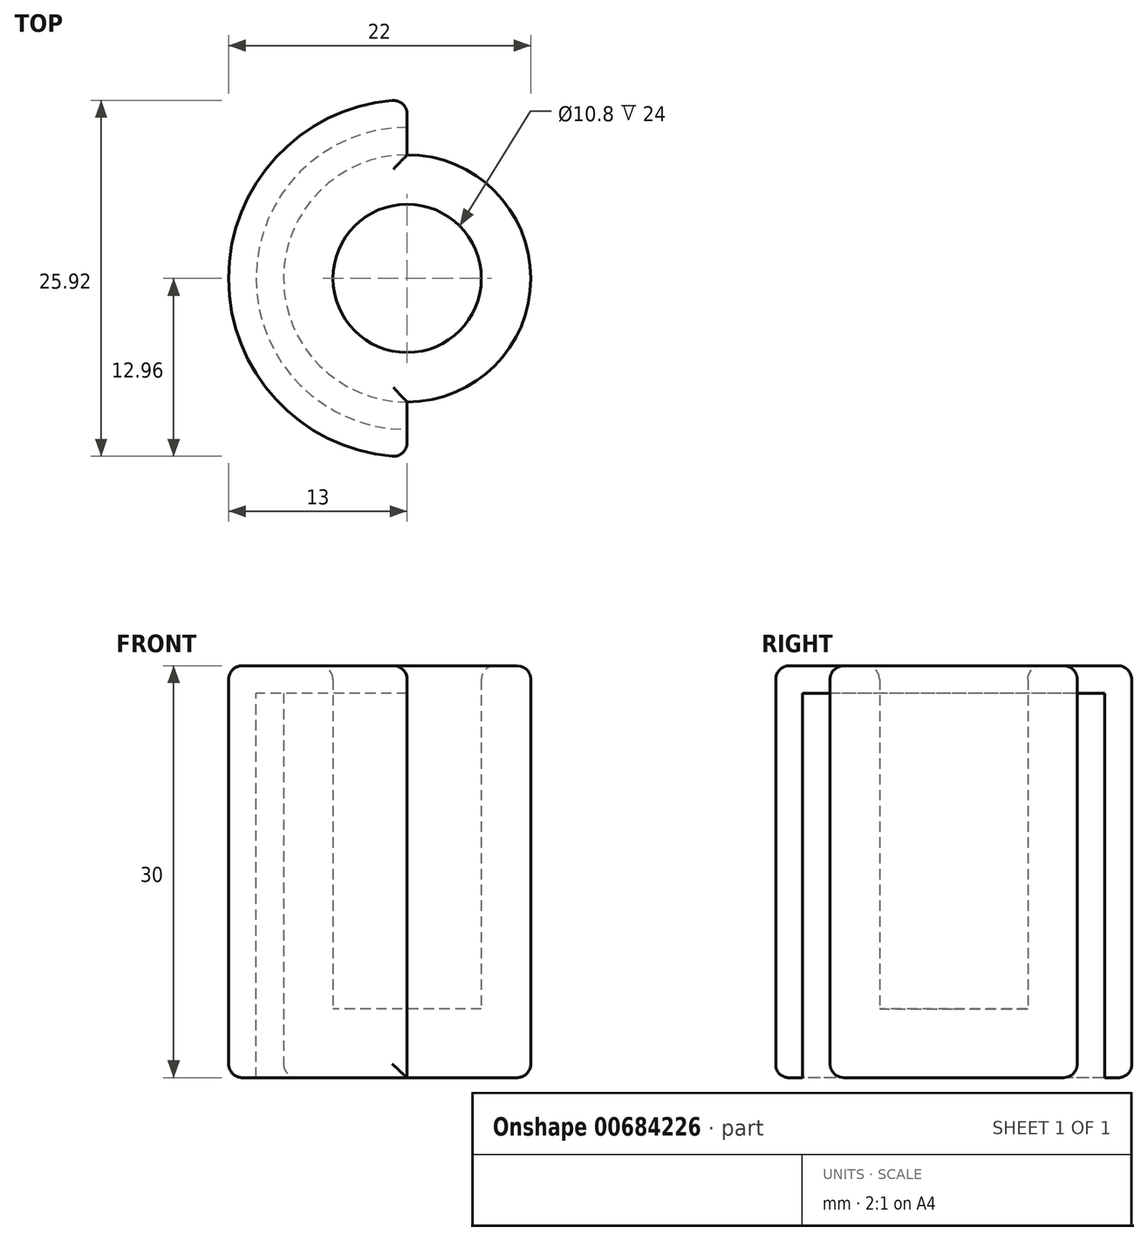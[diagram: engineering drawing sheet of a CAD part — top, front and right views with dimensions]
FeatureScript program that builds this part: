
annotation { "Feature Type Name" : "Feature", "Feature Type Description" : "" }
export const myFeature = defineFeature(function(context is Context, id is Id, definition is map)
    precondition{}
    {
        {
            var Q0;
            Q0=qCreatedBy(makeId("Top.planeOp"),FACE);
            var sketch = newSketch(context, id + "F0", { "sketchPlane" : qUnion([Q0])});
            skCircle(sketch, "E0", {"center": v(0, 0) * mm, "radius": 9 * mm});
            skCircle(sketch, "E1", {"center": v(0, 0) * mm, "radius": 5.4 * mm});
            skSolve(sketch);
        }
        {
            var Q0;
            Q0=makeQuery(id+"F0.imprint","IMPRINT",FACE,{"disambiguationData":[TD([[makeQuery(id+"F0.imprint","IMPRINT",EDGE,{"derivedFrom":sQuery(id+"F0.wireOp",EDGE,"E0")}),1.0]])]});
            extrude(context, id + "F1", {"entities" : qUnion([Q0]), "depth" : 30 * mm, "offsetDistance" : 25 * mm});
        }
        {
            var Q0;
            Q0=makeQuery(id+"F0.imprint","IMPRINT",FACE,{"disambiguationData":[TD([[makeQuery(id+"F0.imprint","IMPRINT",EDGE,{"derivedFrom":sQuery(id+"F0.wireOp",EDGE,"E1")}),1.0]])]});
            extrude(context, id + "F2", {"entities" : qUnion([Q0]), "operationType" : NewBodyOperationType.ADD, "depth" : 5 * mm, "offsetDistance" : 25 * mm});
        }
        {
            var Q0;
            Q0=makeQuery(id+"F1.opExtrude","CAP_FACE",FACE,{"disambiguationData":[OSD([sQuery(id+"F0.wireOp",EDGE,"E0"),sQuery(id+"F0.wireOp",EDGE,"E1")])],"isStart":false});
            var sketch = newSketch(context, id + "F3", { "sketchPlane" : qUnion([Q0])});
            skArc(sketch, "E2", {"start": v(0, 13) * mm, "mid": v(-13, 0) * mm, "end": v(0, -13) * mm});
            skArc(sketch, "E3", {"start": v(0, 11) * mm, "mid": v(-11, 0) * mm, "end": v(0, -11) * mm});
            skLineSegment(sketch, "E4", {"start": v(0, -13) * mm, "end": v(0, -9) * mm});
            skLineSegment(sketch, "E5", {"start": v(0, 13) * mm, "end": v(0, 9) * mm});
            skSolve(sketch);
        }
        {
            var Q0;
            Q0=makeQuery(id+"F3.imprint","IMPRINT",FACE,{"disambiguationData":[TD([[makeQuery(id+"F3.imprint","IMPRINT",EDGE,{"derivedFrom":sQuery(id+"F3.wireOp",EDGE,"E2")}),1.0]])]});
            var Q1;
            {var subQ3=sQuery(id+"F3.wireOp",EDGE,"E3");Q1=makeQuery(id+"F3.imprint","IMPRINT",FACE,{"disambiguationData":[TD([[makeQuery(id+"F3.imprint","IMPRINT",EDGE,{"derivedFrom":subQ3}),1.0]])]});}
            extrude(context, id + "F4", {"entities" : qUnion([Q0, Q1]), "operationType" : NewBodyOperationType.ADD, "oppositeDirection" : true, "depth" : 2 * mm, "offsetDistance" : 25 * mm});
        }
        {
            var Q0;
            {var subQ0=sQuery(id+"F3.wireOp",EDGE,"E2");Q0=makeQuery(id+"F3.imprint","IMPRINT",FACE,{"disambiguationData":[TD([[makeQuery(id+"F3.imprint","IMPRINT",EDGE,{"derivedFrom":subQ0}),1.0]])]});}
            extrude(context, id + "F5", {"entities" : qUnion([Q0]), "operationType" : NewBodyOperationType.ADD, "oppositeDirection" : true, "depth" : 30 * mm, "offsetDistance" : 25 * mm});
        }
        {
            var Q0;
            Q0=makeQuery(id+"F1.opExtrude","CAP_EDGE",EDGE,{"disambiguationData":[OSD([sQuery(id+"F0.wireOp",EDGE,"E0")])],"isStart":true});
            var Q1;
            Q1=makeQuery(id+"F5.opExtrude","CAP_EDGE",EDGE,{"disambiguationData":[OSD([sQuery(id+"F3.wireOp",EDGE,"E2")])],"isStart":false});
            var Q2;
            Q2=makeQuery(id+"F4.opExtrude","CAP_EDGE",EDGE,{"disambiguationData":[OSD([sQuery(id+"F3.wireOp",EDGE,"E2")])],"isStart":true});
            var Q3;
            {var subQ0=sQuery(id+"F3.wireOp",EDGE,"E5");var subQ1=sQuery(id+"F3.wireOp",EDGE,"E2");Q3=makeQuery(id+"F5.boolean.opBoolean","MERGE",EDGE,{"derivedFrom":[makeQuery(id+"F4.opExtrude","SWEPT_EDGE",EDGE,{"disambiguationData":[OSD([subQ1,subQ0])]}),makeQuery(id+"F5.opExtrude","SWEPT_EDGE",EDGE,{"disambiguationData":[OSD([subQ1,subQ0])]})]});}
            var Q4;
            {var subQ0=sQuery(id+"F3.wireOp",EDGE,"E4");var subQ1=sQuery(id+"F3.wireOp",EDGE,"E2");Q4=makeQuery(id+"F5.boolean.opBoolean","MERGE",EDGE,{"derivedFrom":[makeQuery(id+"F4.opExtrude","SWEPT_EDGE",EDGE,{"disambiguationData":[OSD([subQ1,subQ0])]}),makeQuery(id+"F5.opExtrude","SWEPT_EDGE",EDGE,{"disambiguationData":[OSD([subQ1,subQ0])]})]});}
            var Q5;
            Q5=makeQuery(id+"F4.opExtrude","CAP_EDGE",EDGE,{"disambiguationData":[OSD([sQuery(id+"F3.wireOp",EDGE,"E4")])],"isStart":true});
            var Q6;
            Q6=makeQuery(id+"F4.opExtrude","CAP_EDGE",EDGE,{"disambiguationData":[OSD([sQuery(id+"F3.wireOp",EDGE,"E5")])],"isStart":true});
            var Q7;
            Q7=makeQuery(id+"F1.opExtrude","CAP_EDGE",EDGE,{"disambiguationData":[OSD([sQuery(id+"F0.wireOp",EDGE,"E0")])],"isStart":false});
            var Q8;
            Q8=makeQuery(id+"F1.opExtrude","CAP_EDGE",EDGE,{"disambiguationData":[OSD([sQuery(id+"F0.wireOp",EDGE,"E1")])],"isStart":false});
            fillet(context, id + "F6", {"entities" : qUnion([Q0, Q1, Q2, Q3, Q4, Q5, Q6, Q7, Q8]), "radius" : 1 * mm, "allowEdgeOverflow" : false});
        }
    });
